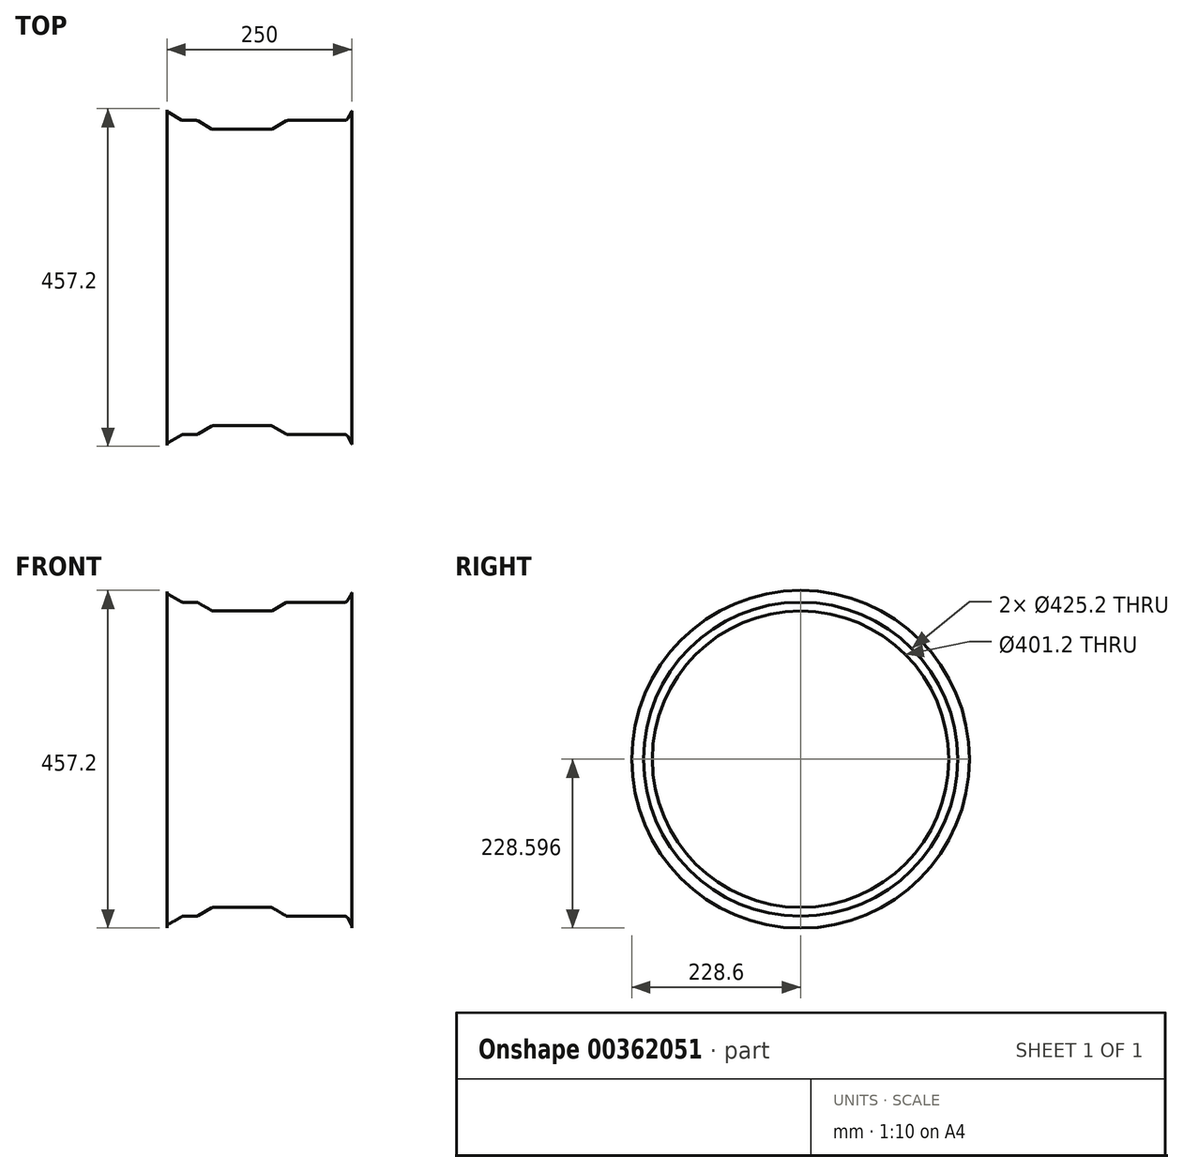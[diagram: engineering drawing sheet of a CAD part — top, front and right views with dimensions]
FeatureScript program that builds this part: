
annotation { "Feature Type Name" : "Feature", "Feature Type Description" : "" }
export const myFeature = defineFeature(function(context is Context, id is Id, definition is map)
    precondition{}
    {
        {
            var Q0;
            Q0=qCreatedBy(makeId("Front.planeOp"),FACE);
            var sketch = newSketch(context, id + "F0", { "sketchPlane" : qUnion([Q0])});
            skLineSegment(sketch, "E0", {"start": v(-82.46, 72.8) * mm, "end": v(-82.46, 68.8) * mm});
            skLineSegment(sketch, "E1", {"start": v(-82.46, 68.8) * mm, "end": v(-61.68, 56.8) * mm});
            skLineSegment(sketch, "E2", {"start": v(-61.68, 56.8) * mm, "end": v(-82.46, 68.8) * mm});
            skLineSegment(sketch, "E3", {"start": v(-61.68, 56.8) * mm, "end": v(-41.68, 56.8) * mm});
            skLineSegment(sketch, "E4", {"start": v(-41.68, 56.8) * mm, "end": v(-20.9, 44.8) * mm});
            skLineSegment(sketch, "E5", {"start": v(-20.9, 44.8) * mm, "end": v(59.1, 44.8) * mm});
            skLineSegment(sketch, "E6", {"start": v(59.1, 44.8) * mm, "end": v(79.89, 56.8) * mm});
            skLineSegment(sketch, "E7", {"start": v(79.89, 56.8) * mm, "end": v(59.1, 44.8) * mm});
            skLineSegment(sketch, "E8", {"start": v(167.54, 68.8) * mm, "end": v(167.54, 72.8) * mm});
            skPoint(sketch, "E9.end.orphan", {"position": v(79.89, 44.8) * mm});
            skPoint(sketch, "E10.start.orphan", {"position": v(-82.46, 59.67) * mm});
            skLineSegment(sketch, "E11", {"start": v(79.89, 56.8) * mm, "end": v(160.6, 56.8) * mm});
            skLineSegment(sketch, "E12", {"start": v(160.6, 56.8) * mm, "end": v(167.54, 68.8) * mm});
            skLineSegment(sketch, "E13", {"start": v(-82.46, -155.8) * mm, "end": v(167.54, -155.8) * mm, "construction": true});
            skSolve(sketch);
        }
        {
            var Q0;
            Q0=qSketchRegion(id+"F0",true);
            var Q1;
            Q1=sQuery(id+"F0.wireOp",EDGE,"E0");
            var Q2;
            Q2=sQuery(id+"F0.wireOp",EDGE,"E2");
            var Q3;
            Q3=sQuery(id+"F0.wireOp",EDGE,"E3");
            var Q4;
            Q4=sQuery(id+"F0.wireOp",EDGE,"E4");
            var Q5;
            Q5=sQuery(id+"F0.wireOp",EDGE,"E5");
            var Q6;
            Q6=sQuery(id+"F0.wireOp",EDGE,"E7");
            var Q7;
            Q7=sQuery(id+"F0.wireOp",EDGE,"E11");
            var Q8;
            Q8=sQuery(id+"F0.wireOp",EDGE,"E12");
            var Q9;
            Q9=sQuery(id+"F0.wireOp",EDGE,"E8");
            var Q10;
            Q10=sQuery(id+"F0.wireOp",EDGE,"E13");
            revolve(context, id + "F1", {"bodyType" : ToolBodyType.SURFACE, "entities" : qUnion([Q0]), "surfaceEntities" : qUnion([Q1, Q2, Q3, Q4, Q5, Q6, Q7, Q8, Q9]), "axis" : qUnion([Q10]), "revolveType" : RevolveType.FULL});
        }
        {
            var Q0;
            Q0=makeQuery(id+"F1.opRevolve","SWEPT_FACE",FACE,{"disambiguationData":[OSD([sQuery(id+"F0.wireOp",EDGE,"E5")])]});
            var Q1;
            Q1=makeQuery(id+"F1.opRevolve","SWEPT_FACE",FACE,{"disambiguationData":[OSD([sQuery(id+"F0.wireOp",EDGE,"E11")])]});
            var Q2;
            Q2=makeQuery(id+"F1.opRevolve","SWEPT_EDGE",EDGE,{"disambiguationData":[OSD([sQuery(id+"F0.wireOp",VERTEX,"E7.end")])]});
            var Q3;
            Q3=makeQuery(id+"F1.opRevolve","SWEPT_EDGE",EDGE,{"disambiguationData":[OSD([sQuery(id+"F0.wireOp",VERTEX,"E11.start")])]});
            var Q4;
            Q4=makeQuery(id+"F1.opRevolve","SWEPT_EDGE",EDGE,{"disambiguationData":[OSD([sQuery(id+"F0.wireOp",VERTEX,"E5.start")])]});
            var Q5;
            Q5=makeQuery(id+"F1.opRevolve","SWEPT_EDGE",EDGE,{"disambiguationData":[OSD([sQuery(id+"F0.wireOp",VERTEX,"E4.start")])]});
            var Q6;
            Q6=makeQuery(id+"F1.opRevolve","SWEPT_EDGE",EDGE,{"disambiguationData":[OSD([sQuery(id+"F0.wireOp",VERTEX,"E3.start")])]});
            var Q7;
            Q7=makeQuery(id+"F1.opRevolve","SWEPT_EDGE",EDGE,{"disambiguationData":[OSD([sQuery(id+"F0.wireOp",VERTEX,"E2.end")])]});
            var Q8;
            Q8=makeQuery(id+"F1.opRevolve","SWEPT_EDGE",EDGE,{"disambiguationData":[OSD([sQuery(id+"F0.wireOp",VERTEX,"E8.start")])]});
            var Q9;
            Q9=makeQuery(id+"F1.opRevolve","SWEPT_EDGE",EDGE,{"disambiguationData":[OSD([sQuery(id+"F0.wireOp",VERTEX,"E12.start")])]});
            fillet(context, id + "F2", {"entities" : qUnion([Q0, Q1, Q2, Q3, Q4, Q5, Q6, Q7, Q8, Q9]), "radius" : 4 * mm, "tangentPropagation" : true, "allowEdgeOverflow" : false});
        }
    });
